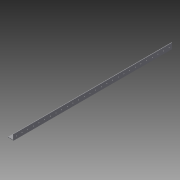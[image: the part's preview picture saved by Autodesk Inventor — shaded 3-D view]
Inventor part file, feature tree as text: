
AUTODESK INVENTOR PART (.ipt)
format: ipt  version: 2015 SP1 (Build 190203100, 203)  size: 155,648 bytes
history: native  units: in
note: dims shown in document units (in); Inventor stores cm internally (conversion verified against a paired STEP export)
features: sketch x4, extrude x2, hole x2, pattern_linear x2, projected_geometry x2, reference x1
ambient origin geometry x8: Origin, YZ Plane, XZ Plane, XY Plane, X Axis, Y Axis, Z Axis, Center Point
bodies: Solid1 (feature_tree)
feature tree (13):
  extrude  "Extrusion1"  Depth=0.09in
  hole  "Hole1"  [1 undecoded]
  pattern_linear  "Rectangular Pattern1"  Spacing1=0.5in  [1 undecoded]
  hole  "Hole2"  [1 undecoded]
  pattern_linear  "Rectangular Pattern2"  Spacing1=0.5in  [1 undecoded]
  extrude  "Extrusion2"  Depth=28.0in
  sketch  "Sketch1"  dims[d0=1.0in d1=0.09in]
  sketch  "Sketch2"  dims[d2=0.09in d3=1.0in]
  projected_geometry  "Projected Loop1"
  sketch  "Sketch3"  dims[d4=28.0in d5=0.0in]
  projected_geometry  "Projected Loop2"
  sketch  "Sketch4"  dims[d6=0.5in d7=0.5in d8=0.1562in d9=0.75in d10=0.375in d11=0.25in d12=0.5635in d13=1.0in d14=0.8108in d15=11.0236in d17=1.0in d18=0.5in d19=0.5in d20=0.1562in d21=0.75in d22=0.375in d23=0.25in d24=0.5635in d25=1.0in d26=0.8108in d27=11.0236in d29=1.0in d30=28.0in d31=0.0in]
  reference  "Reference1"
note: 4 required parameter values undecoded (feature->parameter linkage not recoverable at this tier; creation-order binding heuristic only, values carry confidence <= 0.55)
